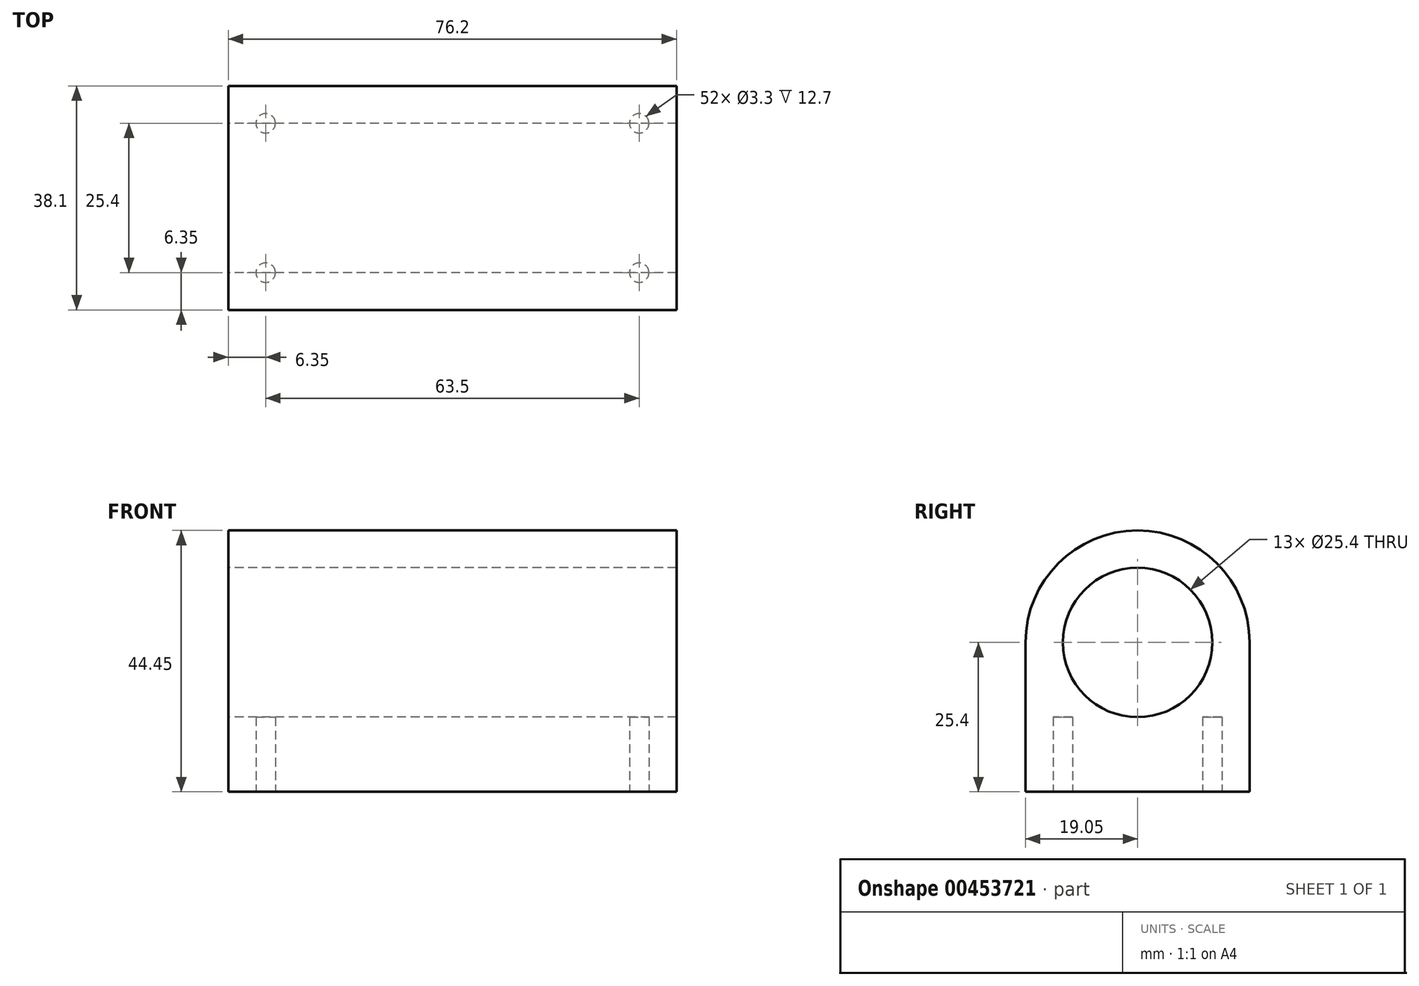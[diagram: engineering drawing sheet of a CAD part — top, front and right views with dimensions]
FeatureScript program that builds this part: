
annotation { "Feature Type Name" : "Feature", "Feature Type Description" : "" }
export const myFeature = defineFeature(function(context is Context, id is Id, definition is map)
    precondition{}
    {
        {
            var Q0;
            Q0=qCreatedBy(makeId("Right.planeOp"),FACE);
            var sketch = newSketch(context, id + "F0", { "sketchPlane" : qUnion([Q0])});
            skLineSegment(sketch, "E0.top", {"start": v(-19.05, -12.7) * mm, "end": v(19.05, -12.7) * mm});
            skLineSegment(sketch, "E0.left", {"start": v(-19.05, 12.7) * mm, "end": v(-19.05, -12.7) * mm});
            skLineSegment(sketch, "E0.right", {"start": v(19.05, 12.7) * mm, "end": v(19.05, -12.7) * mm});
            skArc(sketch, "E1", {"start": v(19.05, 12.7) * mm, "mid": v(0, 31.75) * mm, "end": v(-19.05, 12.7) * mm});
            skCircle(sketch, "E2", {"center": v(0, 12.7) * mm, "radius": 12.7 * mm});
            skSolve(sketch);
        }
        {
            var Q0;
            Q0=makeQuery(id+"F0.imprint","IMPRINT",FACE,{"disambiguationData":[TD([[makeQuery(id+"F0.imprint","IMPRINT",EDGE,{"derivedFrom":sQuery(id+"F0.wireOp",EDGE,"E0.top")}),1.0]])]});
            extrude(context, id + "F1", {"entities" : qUnion([Q0]), "depth" : 76.2 * mm});
        }
        {
            var Q0;
            Q0=makeQuery(id+"F1.opExtrude","SWEPT_FACE",FACE,{"disambiguationData":[OSD([sQuery(id+"F0.wireOp",EDGE,"E0.top")])]});
            var sketch = newSketch(context, id + "F2", { "sketchPlane" : qUnion([Q0])});
            skCircle(sketch, "E3", {"center": v(6.35, 12.7) * mm, "radius": 1.65 * mm});
            skCircle(sketch, "E4", {"center": v(6.35, -12.7) * mm, "radius": 1.65 * mm});
            skCircle(sketch, "E5", {"center": v(69.85, 12.7) * mm, "radius": 1.65 * mm});
            skCircle(sketch, "E6", {"center": v(69.85, -12.7) * mm, "radius": 1.65 * mm});
            skSolve(sketch);
        }
        {
            var Q0;
            Q0=makeQuery(id+"F2.imprint","IMPRINT",FACE,{"disambiguationData":[TD([[makeQuery(id+"F2.imprint","IMPRINT",EDGE,{"derivedFrom":sQuery(id+"F2.wireOp",EDGE,"E3")}),1.0]])]});
            var Q1;
            Q1=makeQuery(id+"F2.imprint","IMPRINT",FACE,{"disambiguationData":[TD([[makeQuery(id+"F2.imprint","IMPRINT",EDGE,{"derivedFrom":sQuery(id+"F2.wireOp",EDGE,"E4")}),1.0]])]});
            var Q2;
            Q2=makeQuery(id+"F2.imprint","IMPRINT",FACE,{"disambiguationData":[TD([[makeQuery(id+"F2.imprint","IMPRINT",EDGE,{"derivedFrom":sQuery(id+"F2.wireOp",EDGE,"E6")}),1.0]])]});
            var Q3;
            Q3=makeQuery(id+"F2.imprint","IMPRINT",FACE,{"disambiguationData":[TD([[makeQuery(id+"F2.imprint","IMPRINT",EDGE,{"derivedFrom":sQuery(id+"F2.wireOp",EDGE,"E5")}),1.0]])]});
            extrude(context, id + "F3", {"entities" : qUnion([Q0, Q1, Q2, Q3]), "operationType" : NewBodyOperationType.REMOVE, "oppositeDirection" : true, "depth" : 12.7 * mm});
        }
    });
